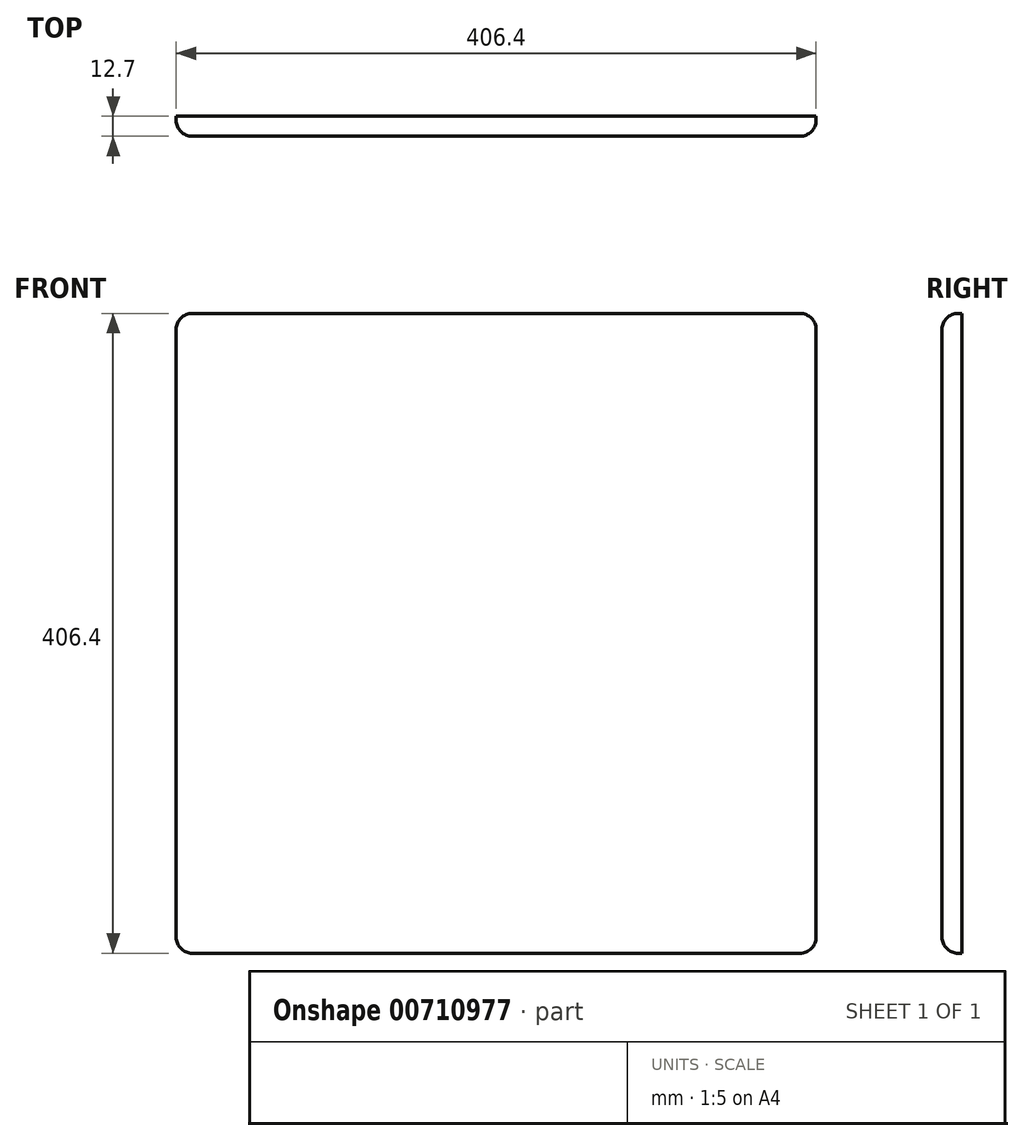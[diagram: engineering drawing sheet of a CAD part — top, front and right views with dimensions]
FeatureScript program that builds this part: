
annotation { "Feature Type Name" : "Feature", "Feature Type Description" : "" }
export const myFeature = defineFeature(function(context is Context, id is Id, definition is map)
    precondition{}
    {
        {
            var Q0;
            Q0=qCreatedBy(makeId("Front.planeOp"),FACE);
            var sketch = newSketch(context, id + "F0", { "sketchPlane" : qUnion([Q0])});
            skLineSegment(sketch, "E0.bottom", {"start": v(-203.2, -203.2) * mm, "end": v(203.2, -203.2) * mm});
            skLineSegment(sketch, "E0.top", {"start": v(-203.2, 203.2) * mm, "end": v(203.2, 203.2) * mm});
            skLineSegment(sketch, "E0.left", {"start": v(-203.2, -203.2) * mm, "end": v(-203.2, 203.2) * mm});
            skLineSegment(sketch, "E0.right", {"start": v(203.2, -203.2) * mm, "end": v(203.2, 203.2) * mm});
            skSolve(sketch);
        }
        {
            var Q0;
            Q0=makeQuery(id+"F0.imprint","IMPRINT",FACE,{"disambiguationData":[TD([[makeQuery(id+"F0.imprint","IMPRINT",EDGE,{"derivedFrom":sQuery(id+"F0.wireOp",EDGE,"E0.bottom")}),1.0]])]});
            extrude(context, id + "F1", {"entities" : qUnion([Q0]), "endBound" : BoundingType.SYMMETRIC, "depth" : 12.7 * mm, "offsetDistance" : 25.4 * mm});
        }
        {
            var Q0;
            Q0=makeQuery(id+"F1.opExtrude","CAP_EDGE",EDGE,{"disambiguationData":[OSD([sQuery(id+"F0.wireOp",EDGE,"E0.top")])],"isStart":false});
            var Q1;
            Q1=makeQuery(id+"F1.opExtrude","CAP_EDGE",EDGE,{"disambiguationData":[OSD([sQuery(id+"F0.wireOp",EDGE,"E0.left")])],"isStart":false});
            var Q2;
            Q2=makeQuery(id+"F1.opExtrude","CAP_EDGE",EDGE,{"disambiguationData":[OSD([sQuery(id+"F0.wireOp",EDGE,"E0.bottom")])],"isStart":false});
            var Q3;
            Q3=makeQuery(id+"F1.opExtrude","CAP_EDGE",EDGE,{"disambiguationData":[OSD([sQuery(id+"F0.wireOp",EDGE,"E0.right")])],"isStart":false});
            var Q4;
            Q4=makeQuery(id+"F1.opExtrude","SWEPT_EDGE",EDGE,{"disambiguationData":[OSD([sQuery(id+"F0.wireOp",EDGE,"E0.bottom"),sQuery(id+"F0.wireOp",EDGE,"E0.left")])]});
            var Q5;
            Q5=makeQuery(id+"F1.opExtrude","SWEPT_EDGE",EDGE,{"disambiguationData":[OSD([sQuery(id+"F0.wireOp",EDGE,"E0.top"),sQuery(id+"F0.wireOp",EDGE,"E0.left")])]});
            var Q6;
            Q6=makeQuery(id+"F1.opExtrude","SWEPT_EDGE",EDGE,{"disambiguationData":[OSD([sQuery(id+"F0.wireOp",EDGE,"E0.top"),sQuery(id+"F0.wireOp",EDGE,"E0.right")])]});
            var Q7;
            Q7=makeQuery(id+"F1.opExtrude","SWEPT_EDGE",EDGE,{"disambiguationData":[OSD([sQuery(id+"F0.wireOp",EDGE,"E0.bottom"),sQuery(id+"F0.wireOp",EDGE,"E0.right")])]});
            fillet(context, id + "F2", {"entities" : qUnion([Q0, Q1, Q2, Q3, Q4, Q5, Q6, Q7]), "radius" : 10.16 * mm, "tangentPropagation" : true, "allowEdgeOverflow" : false});
        }
    });
